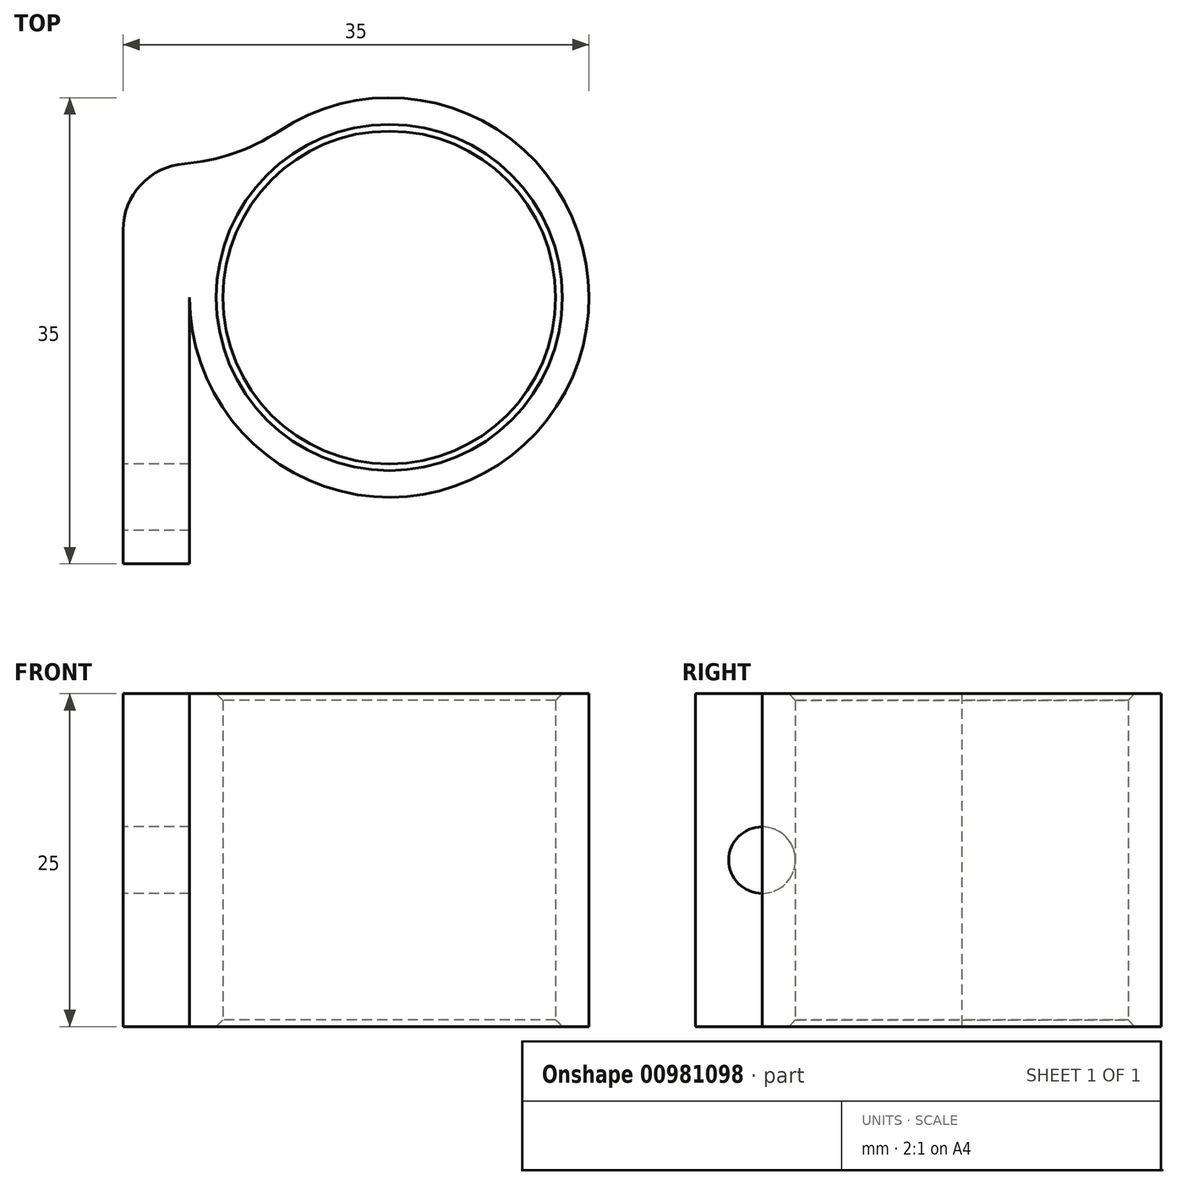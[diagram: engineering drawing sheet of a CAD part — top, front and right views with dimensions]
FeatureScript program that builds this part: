
annotation { "Feature Type Name" : "Feature", "Feature Type Description" : "" }
export const myFeature = defineFeature(function(context is Context, id is Id, definition is map)
    precondition{}
    {
        {
            var Q0;
            Q0=qCreatedBy(makeId("Top.planeOp"),FACE);
            var sketch = newSketch(context, id + "F0", { "sketchPlane" : qUnion([Q0])});
            skCircle(sketch, "E0", {"center": v(0, 0) * mm, "radius": 12.5 * mm});
            skCircle(sketch, "E1", {"center": v(0, 0) * mm, "radius": 15 * mm});
            skLineSegment(sketch, "E2", {"start": v(-15, 0) * mm, "end": v(-20, 0) * mm});
            skLineSegment(sketch, "E3", {"start": v(-20, 0) * mm, "end": v(-20, -20) * mm});
            skLineSegment(sketch, "E4", {"start": v(-20, 0) * mm, "end": v(-20, 10) * mm});
            skLineSegment(sketch, "E5", {"start": v(-20, 10) * mm, "end": v(-11.18, 10) * mm});
            skLineSegment(sketch, "E6", {"start": v(-20, -20) * mm, "end": v(-15, -20) * mm});
            skLineSegment(sketch, "E7", {"start": v(-15, -20) * mm, "end": v(-15, 0) * mm});
            skSolve(sketch);
        }
        {
            var Q0;
            Q0 = qSketchRegion(id + "F0", true);
            extrude(context, id + "F1", {"entities" : qUnion([Q0]), "depth" : 25 * mm, "offsetDistance" : 25 * mm});
        }
        {
            var Q0;
            Q0=makeQuery(id+"F1.opExtrude","SWEPT_EDGE",EDGE,{"disambiguationData":[OSD([sQuery(id+"F0.wireOp",EDGE,"E1"),sQuery(id+"F0.wireOp",EDGE,"E5")])]});
            fillet(context, id + "F2", {"entities" : qUnion([Q0]), "radius" : 15 * mm, "tangentPropagation" : true, "allowEdgeOverflow" : false});
        }
        {
            var Q0;
            Q0=makeQuery(id+"F1.opExtrude","SWEPT_EDGE",EDGE,{"disambiguationData":[OSD([sQuery(id+"F0.wireOp",EDGE,"E4"),sQuery(id+"F0.wireOp",EDGE,"E5")])]});
            fillet(context, id + "F3", {"entities" : qUnion([Q0]), "radius" : 5 * mm, "tangentPropagation" : true, "allowEdgeOverflow" : false});
        }
        {
            var Q0;
            Q0=makeQuery(id+"F1.opExtrude","SWEPT_FACE",FACE,{"disambiguationData":[OSD([sQuery(id+"F0.wireOp",EDGE,"E3"),sQuery(id+"F0.wireOp",EDGE,"E4")])]});
            var sketch = newSketch(context, id + "F4", { "sketchPlane" : qUnion([Q0])});
            skLineSegment(sketch, "E8", {"start": v(20, 12.5) * mm, "end": v(15, 12.5) * mm});
            skCircle(sketch, "E9", {"center": v(15, 12.5) * mm, "radius": 2.5 * mm});
            skSolve(sketch);
        }
        {
            var Q0;
            Q0 = qSketchRegion(id + "F4", true);
            extrude(context, id + "F5", {"entities" : qUnion([Q0]), "operationType" : NewBodyOperationType.REMOVE, "oppositeDirection" : true, "depth" : 5 * mm, "offsetDistance" : 25 * mm});
        }
        {
            var Q0;
            Q0=makeQuery(id+"F1.opExtrude","CAP_EDGE",EDGE,{"disambiguationData":[OSD([sQuery(id+"F0.wireOp",EDGE,"E0")])],"isStart":true});
            var Q1;
            Q1=makeQuery(id+"F1.opExtrude","CAP_EDGE",EDGE,{"disambiguationData":[OSD([sQuery(id+"F0.wireOp",EDGE,"E0")])],"isStart":false});
            chamfer(context, id + "F6", {"entities" : qUnion([Q0, Q1]), "width" : 0.5 * mm, "tangentPropagation" : true});
        }
    });
